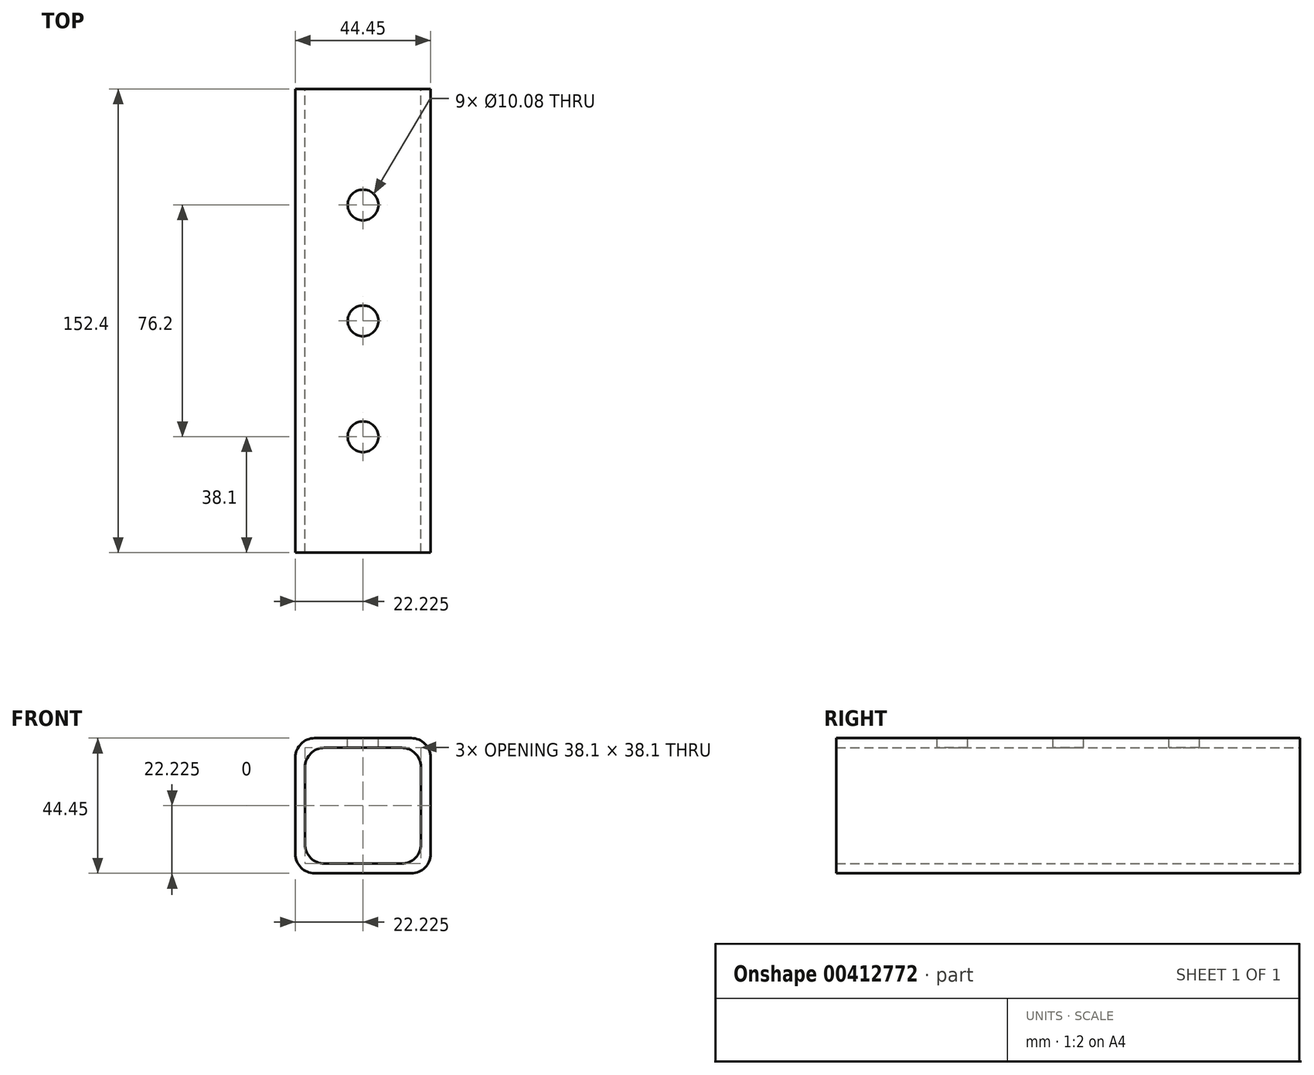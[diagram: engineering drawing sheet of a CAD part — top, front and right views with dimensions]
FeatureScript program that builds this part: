
annotation { "Feature Type Name" : "Feature", "Feature Type Description" : "" }
export const myFeature = defineFeature(function(context is Context, id is Id, definition is map)
    precondition{}
    {
        {
            var Q0;
            Q0=qCreatedBy(makeId("Front.planeOp"),FACE);
            var sketch = newSketch(context, id + "F0", { "sketchPlane" : qUnion([Q0])});
            skLineSegment(sketch, "E0.bottom", {"start": v(6.35, 0) * mm, "end": v(38.1, 0) * mm});
            skLineSegment(sketch, "E0.top", {"start": v(6.35, 44.45) * mm, "end": v(38.1, 44.45) * mm});
            skLineSegment(sketch, "E0.left", {"start": v(0, 6.35) * mm, "end": v(0, 38.1) * mm});
            skLineSegment(sketch, "E0.right", {"start": v(44.45, 6.35) * mm, "end": v(44.45, 38.1) * mm});
            skLineSegment(sketch, "E1.bottom", {"start": v(9.52, 3.18) * mm, "end": v(34.92, 3.18) * mm});
            skLineSegment(sketch, "E1.top", {"start": v(9.52, 41.27) * mm, "end": v(34.92, 41.27) * mm});
            skLineSegment(sketch, "E1.left", {"start": v(3.17, 9.52) * mm, "end": v(3.17, 34.92) * mm});
            skLineSegment(sketch, "E1.right", {"start": v(41.27, 9.53) * mm, "end": v(41.27, 34.92) * mm});
            skPoint(sketch, "E2.visualSharp", {"position": v(44.45, 44.45) * mm});
            skArc(sketch, "E2.filletArc", {"start": v(44.45, 38.1) * mm, "mid": v(42.6, 42.6) * mm, "end": v(38.1, 44.45) * mm});
            skPoint(sketch, "E3.visualSharp", {"position": v(0, 44.45) * mm});
            skArc(sketch, "E3.filletArc", {"start": v(6.35, 44.45) * mm, "mid": v(1.86, 42.6) * mm, "end": v(0, 38.1) * mm});
            skPoint(sketch, "E4.visualSharp", {"position": v(0, 0) * mm});
            skArc(sketch, "E4.filletArc", {"start": v(0, 6.35) * mm, "mid": v(1.86, 1.86) * mm, "end": v(6.35, 0) * mm});
            skPoint(sketch, "E5.visualSharp", {"position": v(3.17, 3.18) * mm});
            skArc(sketch, "E5.filletArc", {"start": v(3.17, 9.52) * mm, "mid": v(5.03, 5.03) * mm, "end": v(9.52, 3.18) * mm});
            skPoint(sketch, "E6.visualSharp", {"position": v(41.27, 3.18) * mm});
            skArc(sketch, "E6.filletArc", {"start": v(34.92, 3.18) * mm, "mid": v(39.42, 5.03) * mm, "end": v(41.27, 9.53) * mm});
            skPoint(sketch, "E7.visualSharp", {"position": v(41.27, 41.27) * mm});
            skArc(sketch, "E7.filletArc", {"start": v(41.27, 34.92) * mm, "mid": v(39.42, 39.42) * mm, "end": v(34.92, 41.27) * mm});
            skPoint(sketch, "E8.visualSharp", {"position": v(3.17, 41.27) * mm});
            skArc(sketch, "E8.filletArc", {"start": v(9.52, 41.27) * mm, "mid": v(5.03, 39.42) * mm, "end": v(3.17, 34.92) * mm});
            skPoint(sketch, "E9.visualSharp", {"position": v(44.45, 0) * mm});
            skArc(sketch, "E9.filletArc", {"start": v(38.1, 0) * mm, "mid": v(42.6, 1.86) * mm, "end": v(44.45, 6.35) * mm});
            skSolve(sketch);
        }
        {
            var Q0;
            Q0=makeQuery(id+"F0.imprint","IMPRINT",FACE,{"disambiguationData":[TD([[makeQuery(id+"F0.imprint","IMPRINT",EDGE,{"derivedFrom":sQuery(id+"F0.wireOp",EDGE,"E0.bottom")}),1.0]])]});
            extrude(context, id + "F1", {"entities" : qUnion([Q0]), "depth" : 152.4 * mm, "offsetDistance" : 25.4 * mm});
        }
        {
            var Q0;
            Q0=makeQuery(id+"F1.opExtrude","SWEPT_FACE",FACE,{"disambiguationData":[OSD([sQuery(id+"F0.wireOp",EDGE,"E0.top")])]});
            var sketch = newSketch(context, id + "F2", { "sketchPlane" : qUnion([Q0])});
            skPoint(sketch, "E10", {"position": v(22.22, -114.3) * mm});
            skPoint(sketch, "E10.positionSnap0", {"position": v(22.22, -152.4) * mm});
            skPoint(sketch, "E11", {"position": v(22.22, -76.2) * mm});
            skPoint(sketch, "E12", {"position": v(22.22, -38.1) * mm});
            skSolve(sketch);
        }
        {
            var Q0;
            Q0=sQuery(id+"F2.wireOp",VERTEX,"E10");
            var Q1;
            Q1=sQuery(id+"F2.wireOp",VERTEX,"E11");
            var Q2;
            Q2=sQuery(id+"F2.wireOp",VERTEX,"E12");
            var Q3;
            Q3=makeQuery(id+"F1.opExtrude","SWEPT_BODY",BODY,{"disambiguationData":[OSD([sQuery(id+"F0.wireOp",EDGE,"E0.bottom"),sQuery(id+"F0.wireOp",EDGE,"E0.top"),sQuery(id+"F0.wireOp",EDGE,"E0.left"),sQuery(id+"F0.wireOp",EDGE,"E0.right"),sQuery(id+"F0.wireOp",EDGE,"E1.bottom"),sQuery(id+"F0.wireOp",EDGE,"E1.top"),sQuery(id+"F0.wireOp",EDGE,"E1.left"),sQuery(id+"F0.wireOp",EDGE,"E1.right"),sQuery(id+"F0.wireOp",EDGE,"E2.filletArc"),sQuery(id+"F0.wireOp",EDGE,"E3.filletArc"),sQuery(id+"F0.wireOp",EDGE,"E4.filletArc"),sQuery(id+"F0.wireOp",EDGE,"E5.filletArc"),sQuery(id+"F0.wireOp",EDGE,"E6.filletArc"),sQuery(id+"F0.wireOp",EDGE,"E7.filletArc"),sQuery(id+"F0.wireOp",EDGE,"E8.filletArc"),sQuery(id+"F0.wireOp",EDGE,"E9.filletArc")])]});
            hole(context, id + "F3", {"style" : HoleStyle.SIMPLE, "endStyle" : HoleEndStyle.BLIND, "standardTappedOrClearance" : lookupTablePath({ "standard" : "ANSI", "fit" : "Normal (ASME)", "size" : "3/8", "type" : "Clearance" }), "standardBlindInLast" : lookupTablePath({ "fit" : "Free", "standard" : "ANSI", "size" : "3/8", "type" : "Clearance" }), "holeDiameter" : 10.08 * mm, "holeDepth" : 12.7 * mm, "tappedDepth" : 20.65 * mm, "tapClearance" : 3, "startFromSketch" : true, "locations" : qUnion([Q0, Q1, Q2]), "scope" : qUnion([Q3])});
        }
    });
